# Revit family: Контроллер-Ех взрывозащищенный Z-R5 АЯКС
name_source: partatom
category: Датчики
units: mm (PartAtom-declared; Revit-internal decimal feet)

## family parameters
Всегда вертикально = Да
Заголовок OmniClass = Communication and Data Processing Equipment
На основе рабочей плоскости = Нет
Номер OmniClass = 23.85.50.17
Общий = Нет
При загрузке вырезать с полостями = Нет
Размер круглого соединителя = Использовать диаметр
Сохранять ориентацию аннотаций = Нет
Тип детали = Нормальный
Точка принадлежности помещению = Нет

## types (1)
- Контроллер-Ех взрывозащищенный Z-R5 АЯКС
    ADSK_Единица измерения = шт.
    ADSK_Завод-изготовитель = ООО НПП «МАГНИТО-КОНТАКТ»
    ADSK_Масса = 1.3
    ADSK_Материал = Алюминиевый сплав
    ADSK_Наименование = Контроллер-Ех взрывозащищенный Z-R5 АЯКС
    ADSK_Обозначение = АТФЕ.421457.217ПС
    ADSK_Примечание = При подключении считывателя (контактора) к контроллеру следует использовать кабель с витыми парами, например, UTP CAT5, для защиты от помех. При подключении считывателя по протоколу iButton один провод витой пары соединяет клеммы GND контроллера и считывателя. Второй провод этой же витой пары используется для передачи сигнала и соединяет выход считывателя с клеммой контроллера
    ADSK_Размер_Высота = 85 мм
    ADSK_Размер_Длина = 210 мм
    ADSK_Размер_Ширина = 160 мм
    URL = https://m-kontakt.ru
    Атмосферное давление, кПа = от 84 до 106.7
    Выход для подключения замка = реле (тип 1С)
    Изготовитель = ООО НПП «МАГНИТО-КОНТАКТ»
    Кабельный ввод = Да
    Климатическое исполнение по ГОСТ 15150 = УХЛ3.1
    Количество ключей/карт (max), шт = 1364
    Левый кабельный ввод = Да
    Напряжение питания постоянного тока, В = 9-24
    Описание = Контроллер-Ех взрывозащищенный Z-R5 АЯКС предназначен для применения в системах безопасности объектов и сетевых системах контроля и управления доступом (СКУД), в качестве автономного контроллера с силовым реле на выходе для управления внешними устройствами. В качестве входных устройств допускается подключение бесконтактного считывателя карт (рекомендован Считыватель-Ех взрывозащищенный RD-26 АЯКС) эмулирующего протокол iButton (Dallas Touch Memory) или Wiegand (26-42 бит) или контактора ключей Dallas Touch Memory (ключи DS1990A ).
    Отметка по умолчанию = 0 мм
    Поддержка ключа DS1996L = да
    Потребление тока макс, мА = 45
    Правый кабельный ввод = Да
    Протокол подключения внешнего считывателя = iButton, Wiegand-26..42
    Рабочая температура °С = от -40 до +60
    Средний срок службы, лет, не менее = 8
    Степень защиты обеспечиваемая оболочкой = IP66/IP68
    Ток коммутации (24В /120В АС), А = 3
    Установка длительности открывания замка, с = 0 до 220 (заводское значение - 3)
